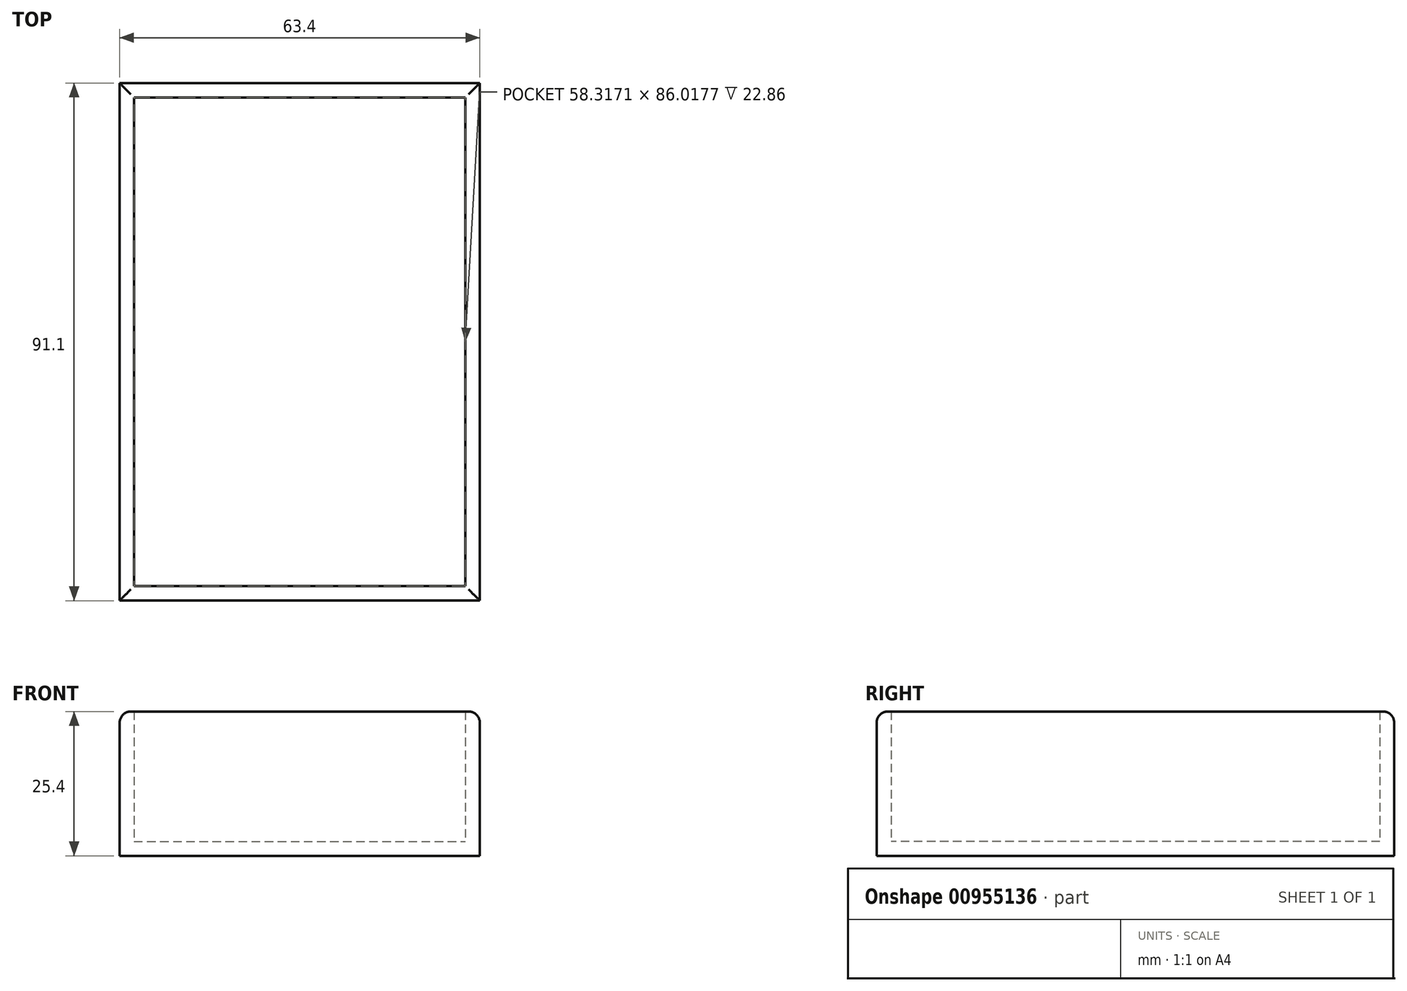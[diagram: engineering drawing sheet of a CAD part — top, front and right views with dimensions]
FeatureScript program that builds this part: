
annotation { "Feature Type Name" : "Feature", "Feature Type Description" : "" }
export const myFeature = defineFeature(function(context is Context, id is Id, definition is map)
    precondition{}
    {
        {
            var Q0;
            Q0=qCreatedBy(makeId("Top.planeOp"),FACE);
            var sketch = newSketch(context, id + "F0", { "sketchPlane" : qUnion([Q0])});
            skLineSegment(sketch, "E0.bottom", {"start": v(-36.7, 49.26) * mm, "end": v(26.7, 49.26) * mm});
            skLineSegment(sketch, "E0.top", {"start": v(-36.7, -41.84) * mm, "end": v(26.7, -41.84) * mm});
            skLineSegment(sketch, "E0.left", {"start": v(-36.7, 49.26) * mm, "end": v(-36.7, -41.84) * mm});
            skLineSegment(sketch, "E0.right", {"start": v(26.7, 49.26) * mm, "end": v(26.7, -41.84) * mm});
            skSolve(sketch);
        }
        {
            var Q0;
            Q0=makeQuery(id+"F0.imprint","IMPRINT",FACE,{"disambiguationData":[TD([[makeQuery(id+"F0.imprint","IMPRINT",EDGE,{"derivedFrom":sQuery(id+"F0.wireOp",EDGE,"E0.bottom")}),-1.0]])]});
            extrude(context, id + "F1", {"entities" : qUnion([Q0]), "depth" : 25.4 * mm, "offsetDistance" : 25.4 * mm});
        }
        {
            var Q0;
            Q0=makeQuery(id+"F1.opExtrude","CAP_FACE",FACE,{"disambiguationData":[OSD([sQuery(id+"F0.wireOp",EDGE,"E0.bottom"),sQuery(id+"F0.wireOp",EDGE,"E0.top"),sQuery(id+"F0.wireOp",EDGE,"E0.left"),sQuery(id+"F0.wireOp",EDGE,"E0.right")])],"isStart":false});
            shell(context, id + "F2", {"entities" : qUnion([Q0]), "thickness" : 2.54 * mm});
        }
        {
            var Q0;
            Q0=makeQuery(id+"F1.opExtrude","CAP_EDGE",EDGE,{"disambiguationData":[OSD([sQuery(id+"F0.wireOp",EDGE,"E0.right")])],"isStart":false});
            var Q1;
            Q1=makeQuery(id+"F1.opExtrude","CAP_EDGE",EDGE,{"disambiguationData":[OSD([sQuery(id+"F0.wireOp",EDGE,"E0.top")])],"isStart":false});
            var Q2;
            Q2=makeQuery(id+"F1.opExtrude","CAP_EDGE",EDGE,{"disambiguationData":[OSD([sQuery(id+"F0.wireOp",EDGE,"E0.left")])],"isStart":false});
            var Q3;
            Q3=makeQuery(id+"F1.opExtrude","CAP_EDGE",EDGE,{"disambiguationData":[OSD([sQuery(id+"F0.wireOp",EDGE,"E0.bottom")])],"isStart":false});
            fillet(context, id + "F3", {"entities" : qUnion([Q0, Q1, Q2, Q3]), "radius" : 2 * mm, "tangentPropagation" : true, "allowEdgeOverflow" : false});
        }
    });
